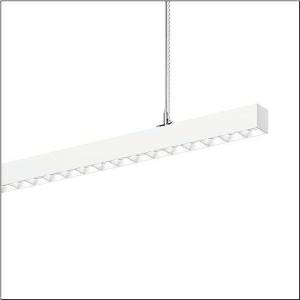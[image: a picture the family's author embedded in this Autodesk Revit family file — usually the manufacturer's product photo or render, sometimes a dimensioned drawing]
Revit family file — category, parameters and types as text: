
# Revit family: silica_r__21_51mx36dc4dwb_53ae
name_source: partatom
category: Lighting Fixtures
units: mm (PartAtom-declared; Revit-internal decimal feet)

## family parameters
Cut with Voids When Loaded = No
Host = Face
Light Source = No
Part Type = Normal
Room Calculation Point = No
Round Connector Dimension = Use Diameter
Shared = No

## types (1)
- --- (1 x LED, 17650 lm, 97.4 W, 4000K)
    Apparent Load = 97 VA
    CIE Flux Codes = 83 98 100 61 100
    Color Rendering = 80
    Color Temperature = 4000K
    Default Elevation = 1800 mm
    Description = Silica® 21, office luminaire, primary light control with darklight reflector, of PMMA, white, CAT 2 (L<= 3000cd/m²), light emission: direct/indirect distribution, primary light characteristic: symmetric, installation type: suspended mounting, LED, rated luminous flux: 17.650lm, luminous efficacy: 181lm/W, light colour: 840, colour temperature: 4000K, control gear: DALI 2, with terminal, 3+2-pole, max. 2.5mm², mains connection: 220..240V, AC, 50/60Hz, rated input power: 97.4W, luminaire housing, of aluminium, traffic white (RAL 9016), length: 3.004mm, width: 53mm, height: 53mm, protection rating (complete): IP20, insulation class (complete): insulation class I (protective earthing), certification: CE, permissible operating ambient temperature: 0..+35°C, standard: EN 50419, packaging unit: 1 piece
    Height = 53 mm
    Lamp = 1 x LED
    Lamp Light Flux = 17650 lm
    Lamp Power = 97.4 W
    Lamp count = 1
    Length = 3004 mm
    Luminous efficacy = 181 lm/W
    Manufacturer = Siteco
    ModVariant = No
    Model = 51MX36DC4DWB
    Mounting Place = Ceiling
    Mounting Type = Pendant
    Number of Poles = 1
    OnlyDefault = Yes
    Power Factor = 1
    Product Name = Silica® 21
    Product group = office luminaire | ceiling pendant
    ProductGroupID = 904
    Protection Class = Protection class I
    Protection Degree = IP 20
    RLX_Detail_Level = 1
    RLX_Emergency_Light_Flux = 0 lm
    RLX_Emergency_Type = 0
    RLX_Emergency_Type_DB = No
    RlxData = <blob elided: 62085 chars, md5=9e2f10c7>
    Socket = socket
    Standby Power = 0 W
    System Light Flux = 17650 lm
    System Power = 97 W
    Type Comments = factory setting: luminous flux: 100 % | dim-lin: 254 | 336 mA
    Type Image = l_1335921.jpg
    URL = http://relux.com
    VarID = @adj_121480
    Voltage = 0 V
    Weight = 0.00 kg
    Width = 53 mm

## geometry (parser evidence)
native form markers: Blend x4, Sweep x14
no freeform markers — native parametric forms only
